# Revit family: Reece_Accessory_Posh_Domaine_Heated Towel Rail_750 mm
name_source: partatom
category: Plumbing Fixtures
revit_build: Autodesk Revit 2018 (Build: 20180329_1100(x64)
units: mm (PartAtom-declared; Revit-internal decimal feet)

## family parameters
Always vertical = Yes
Cut with Voids When Loaded = Yes
Part Type = Normal
Room Calculation Point = Yes
Round Connector Dimension = Use Diameter
Shared = Yes
Work Plane-Based = Yes

## types (2) — shared parameters
Reece_Detail_Additional = Heated Towel Rail
Reece_Detail_Disclaimer = THIS FILE IS THE PROPERTY OF THE REECE GROUP. IT MAY NOT BE REPRODUCED, REVERSE-ENGINEERED OR MODIFIED. ANY REPUBLICATION, TRANSMISSION OR DISTRIBUTION FOR THE PURPOSE OF COMMERCIALLY EXPLOITING THE FILES IS PROHIBITED.
Reece_Material_Main = Reece_Metal_Stainless Steel_Polished
Reece_Overall_Height = 750 mm  [stored 2.46063 ft]
Reece_Overall_Projection = 112 mm  [stored 0.367454 ft]
Reece_Product_Brand = Posh
Reece_Product_Mount = Wall Mounted
Reece_Product_Sub Brand = Domaine
Reece_Product_Type = Accessory
Reece_Product_Web Page = https://www.reece.com.au
zero-valued in all types: Default Elevation

## per-type parameters (varying)
| type | Reece_Overall_Width | Reece_Product_Description | Reece_Product_Number |
| 500 mm x 750 mm_Stainless Steel | 500 mm  [stored 1.64042 ft] | Posh Domaine Heated Towel Rail 500 x 750mm Polished Stainless Steel | 9508099 |
| 700 mm x 750 mm_Stainless Steel | 700 mm  [stored 2.29659 ft] | Posh Domaine Heated Towel Rail 700 x 750mm Polished Stainless Steel | 9506133 |

note: [stored X ft] marks values corroborated as IEEE doubles in the binary element streams (Revit-internal decimal feet)

## geometry (parser evidence)
native form markers: Sweep x4
no freeform markers — native parametric forms only
